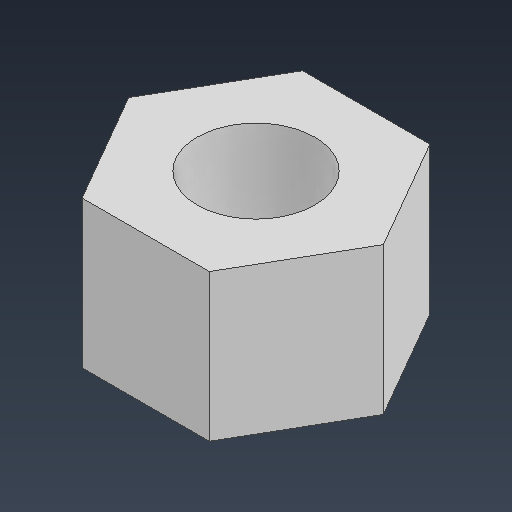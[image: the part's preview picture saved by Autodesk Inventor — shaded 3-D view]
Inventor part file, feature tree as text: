
AUTODESK INVENTOR PART (.ipt)
format: ipt  version: 2025.3 (Build 293356000, 356)  size: 89,600 bytes
history: native  units: mm
features: extrude x1, sketch x1
ambient origin geometry x8: Origin, YZ Plane, XZ Plane, XY Plane, X Axis, Y Axis, Z Axis, Center Point
bodies: Solid1 (feature_tree)
feature tree (2):
  extrude  "Extrusion1"  Depth=4.0mm
  sketch  "Sketch1"  dims[d0=3.2mm d1=3.0mm d2=4.0mm d3=0.0mm]
